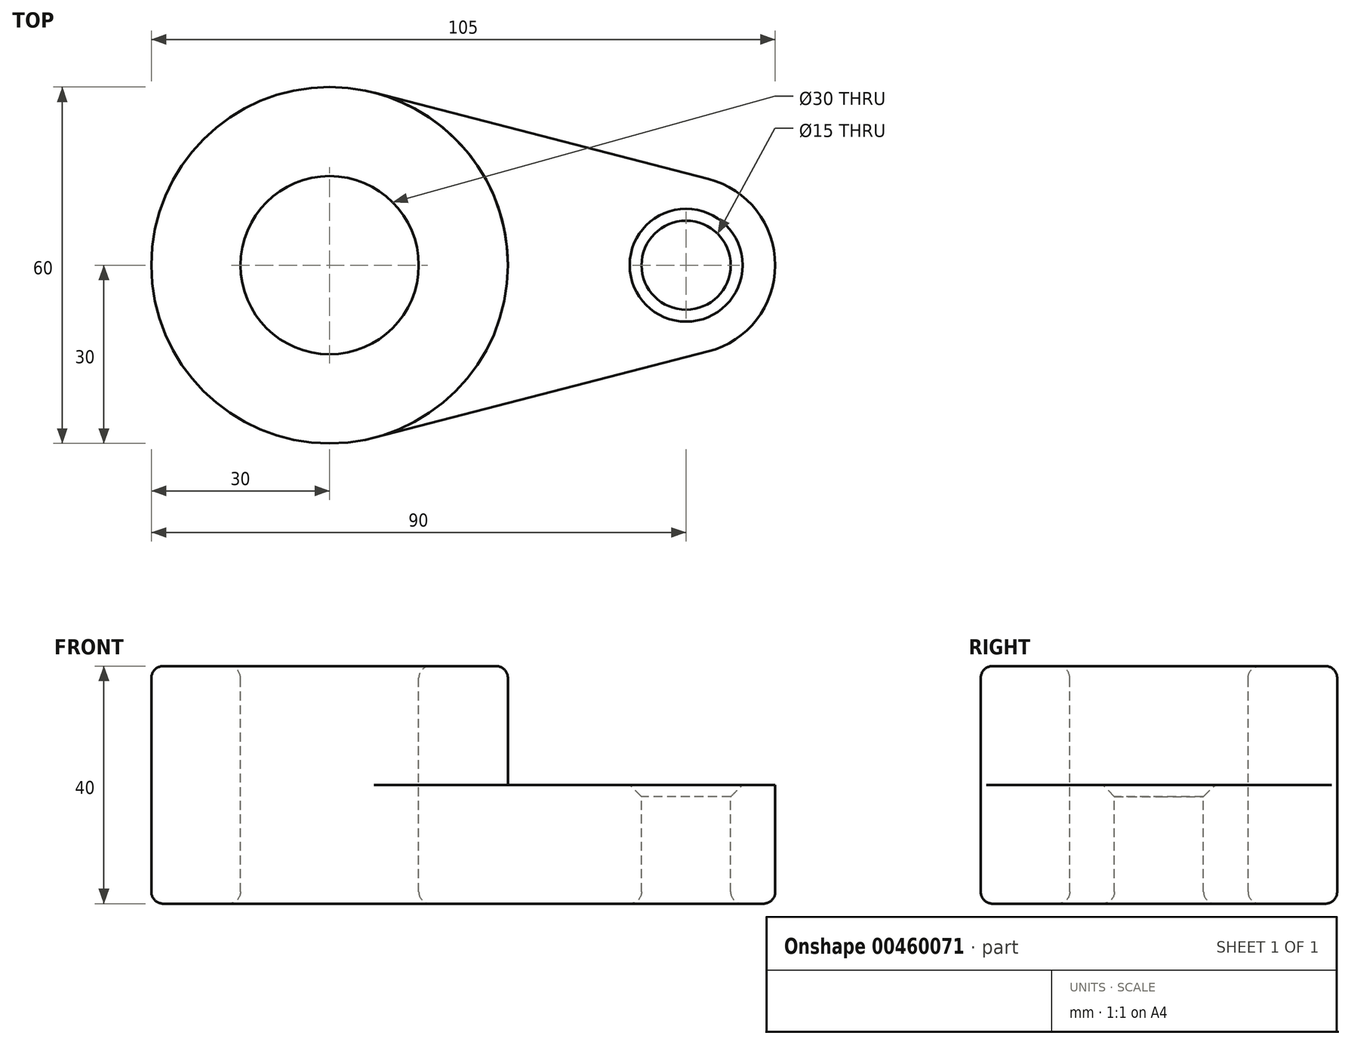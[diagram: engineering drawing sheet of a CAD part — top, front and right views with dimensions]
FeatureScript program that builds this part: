
annotation { "Feature Type Name" : "Feature", "Feature Type Description" : "" }
export const myFeature = defineFeature(function(context is Context, id is Id, definition is map)
    precondition{}
    {
        {
            var Q0;
            Q0=qCreatedBy(makeId("Top.planeOp"),FACE);
            var sketch = newSketch(context, id + "F0", { "sketchPlane" : qUnion([Q0])});
            skCircle(sketch, "E0", {"center": v(0, 0) * mm, "radius": 30 * mm});
            skCircle(sketch, "E1", {"center": v(60, 0) * mm, "radius": 15 * mm});
            skLineSegment(sketch, "E2", {"start": v(7.5, 29.05) * mm, "end": v(63.75, 14.52) * mm});
            skLineSegment(sketch, "E3.MirrorCS", {"start": v(7.5, -29.05) * mm, "end": v(63.75, -14.52) * mm});
            skCircle(sketch, "E4", {"center": v(0, 0) * mm, "radius": 15 * mm});
            skCircle(sketch, "E5", {"center": v(60, 0) * mm, "radius": 7.5 * mm});
            skSolve(sketch);
        }
        {
            var Q0;
            Q0=makeQuery(id+"F0.imprint","IMPRINT",FACE,{"disambiguationData":[TD([[makeQuery(id+"F0.imprint","IMPRINT",EDGE,{"derivedFrom":sQuery(id+"F0.wireOp",EDGE,"E4")}),-1.0]])]});
            var Q1;
            {var subQ0=sQuery(id+"F0.wireOp",EDGE,"E2");Q1=makeQuery(id+"F0.imprint","IMPRINT",FACE,{"disambiguationData":[TD([[makeQuery(id+"F0.imprint","IMPRINT",EDGE,{"derivedFrom":subQ0}),-1.0]])]});}
            var Q2;
            Q2=makeQuery(id+"F0.imprint","IMPRINT",FACE,{"disambiguationData":[TD([[makeQuery(id+"F0.imprint","IMPRINT",EDGE,{"derivedFrom":sQuery(id+"F0.wireOp",EDGE,"E5")}),-1.0]])]});
            extrude(context, id + "F1", {"entities" : qUnion([Q0, Q1, Q2]), "oppositeDirection" : true, "depth" : 20 * mm});
        }
        {
            var Q0;
            Q0=makeQuery(id+"F0.imprint","IMPRINT",FACE,{"disambiguationData":[TD([[makeQuery(id+"F0.imprint","IMPRINT",EDGE,{"derivedFrom":sQuery(id+"F0.wireOp",EDGE,"E4")}),-1.0]])]});
            extrude(context, id + "F2", {"entities" : qUnion([Q0]), "operationType" : NewBodyOperationType.ADD, "depth" : 20 * mm});
        }
        {
            var Q0;
            Q0=makeQuery(id+"F2.opExtrude","CAP_EDGE",EDGE,{"disambiguationData":[OSD([sQuery(id+"F0.wireOp",EDGE,"E0")])],"isStart":false});
            var Q1;
            Q1=makeQuery(id+"F2.opExtrude","CAP_EDGE",EDGE,{"disambiguationData":[OSD([sQuery(id+"F0.wireOp",EDGE,"E4")])],"isStart":false});
            var Q2;
            Q2=makeQuery(id+"F1.opExtrude","CAP_FACE",FACE,{"disambiguationData":[OSD([sQuery(id+"F0.wireOp",EDGE,"E0"),sQuery(id+"F0.wireOp",EDGE,"E1"),sQuery(id+"F0.wireOp",EDGE,"E2"),sQuery(id+"F0.wireOp",EDGE,"E3.MirrorCS"),sQuery(id+"F0.wireOp",EDGE,"E4"),sQuery(id+"F0.wireOp",EDGE,"E5")])],"isStart":false});
            fillet(context, id + "F3", {"entities" : qUnion([Q0, Q1, Q2]), "radius" : 2 * mm, "tangentPropagation" : true, "allowEdgeOverflow" : false});
        }
        {
            var Q0;
            Q0=makeQuery(id+"F1.opExtrude","SWEPT_FACE",FACE,{"disambiguationData":[OSD([sQuery(id+"F0.wireOp",EDGE,"E5")])]});
            chamfer(context, id + "F4", {"entities" : qUnion([Q0]), "width" : 2 * mm, "tangentPropagation" : true});
        }
    });
